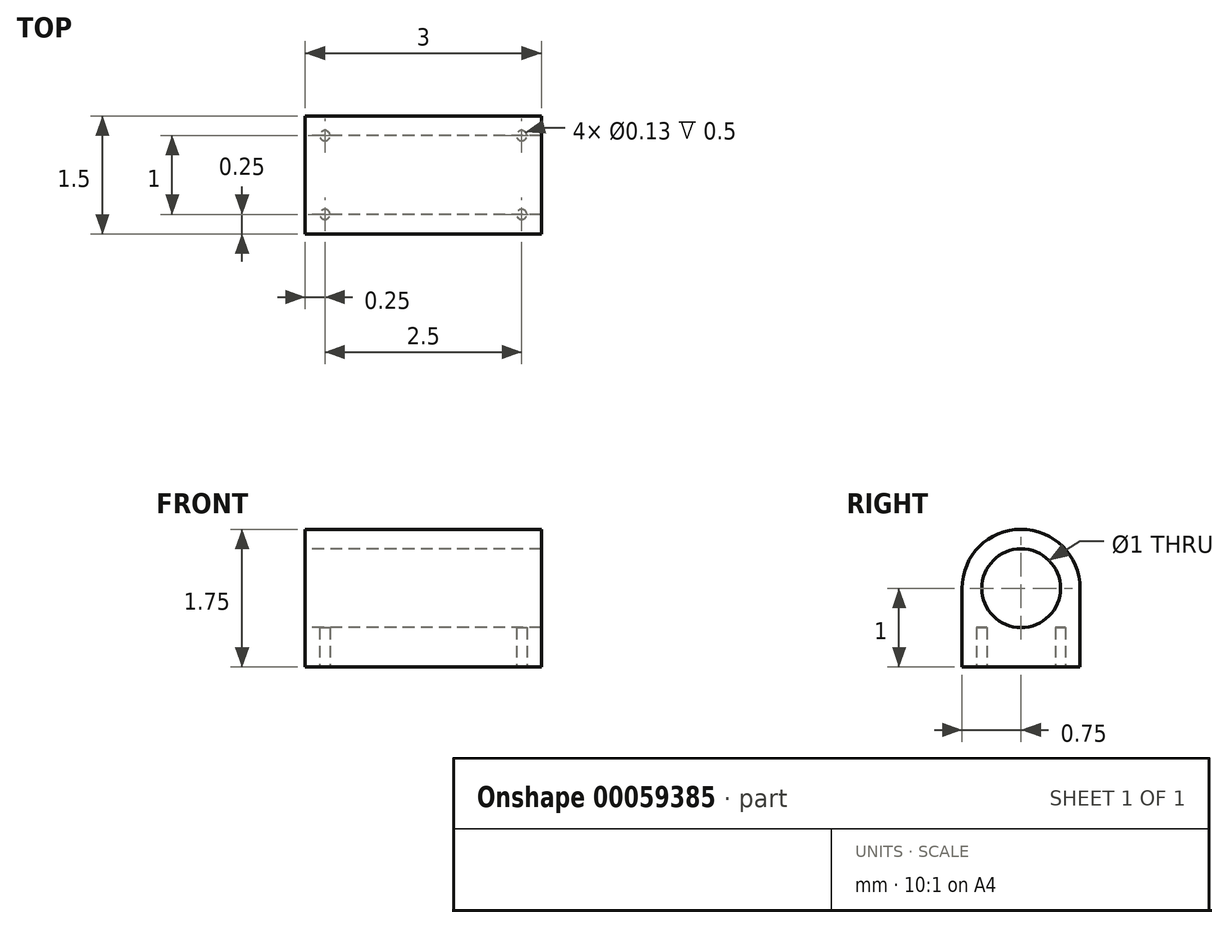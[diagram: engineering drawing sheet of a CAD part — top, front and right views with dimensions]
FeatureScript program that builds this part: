
annotation { "Feature Type Name" : "Feature", "Feature Type Description" : "" }
export const myFeature = defineFeature(function(context is Context, id is Id, definition is map)
    precondition{}
    {
        {
            var Q0;
            Q0=qCreatedBy(makeId("Right.planeOp"),FACE);
            var sketch = newSketch(context, id + "F0", { "sketchPlane" : qUnion([Q0])});
            skCircle(sketch, "E0", {"center": v(0, 0) * mm, "radius": 0.5 * mm});
            skArc(sketch, "E1", {"start": v(0.75, 0) * mm, "mid": v(0, 0.75) * mm, "end": v(-0.75, 0) * mm});
            skLineSegment(sketch, "E2", {"start": v(-0.75, 0) * mm, "end": v(-0.75, -1) * mm});
            skLineSegment(sketch, "E3", {"start": v(-0.75, -1) * mm, "end": v(0.75, -1) * mm});
            skLineSegment(sketch, "E4", {"start": v(0.75, -1) * mm, "end": v(0.75, 0) * mm});
            skSolve(sketch);
        }
        {
            var Q0;
            Q0=makeQuery(id+"F0.imprint","IMPRINT",FACE,{"disambiguationData":[TD([[makeQuery(id+"F0.imprint","IMPRINT",EDGE,{"derivedFrom":sQuery(id+"F0.wireOp",EDGE,"E0")}),-1.0]])]});
            extrude(context, id + "F1", {"entities" : qUnion([Q0]), "endBound" : BoundingType.SYMMETRIC, "depth" : 3 * mm});
        }
        {
            var Q0;
            Q0=makeQuery(id+"F1.opExtrude","SWEPT_FACE",FACE,{"disambiguationData":[OSD([sQuery(id+"F0.wireOp",EDGE,"E3")])]});
            var sketch = newSketch(context, id + "F2", { "sketchPlane" : qUnion([Q0])});
            skCircle(sketch, "E5", {"center": v(1.25, -0.5) * mm, "radius": 0.07 * mm});
            skCircle(sketch, "E6", {"center": v(1.25, 0.5) * mm, "radius": 0.07 * mm});
            skCircle(sketch, "E7", {"center": v(-1.25, -0.5) * mm, "radius": 0.07 * mm});
            skCircle(sketch, "E8", {"center": v(-1.25, 0.5) * mm, "radius": 0.07 * mm});
            skSolve(sketch);
        }
        {
            var Q0;
            Q0 = qSketchRegion(id + "F2", true);
            extrude(context, id + "F3", {"entities" : qUnion([Q0]), "operationType" : NewBodyOperationType.REMOVE, "oppositeDirection" : true, "depth" : 0.5 * mm});
        }
    });
